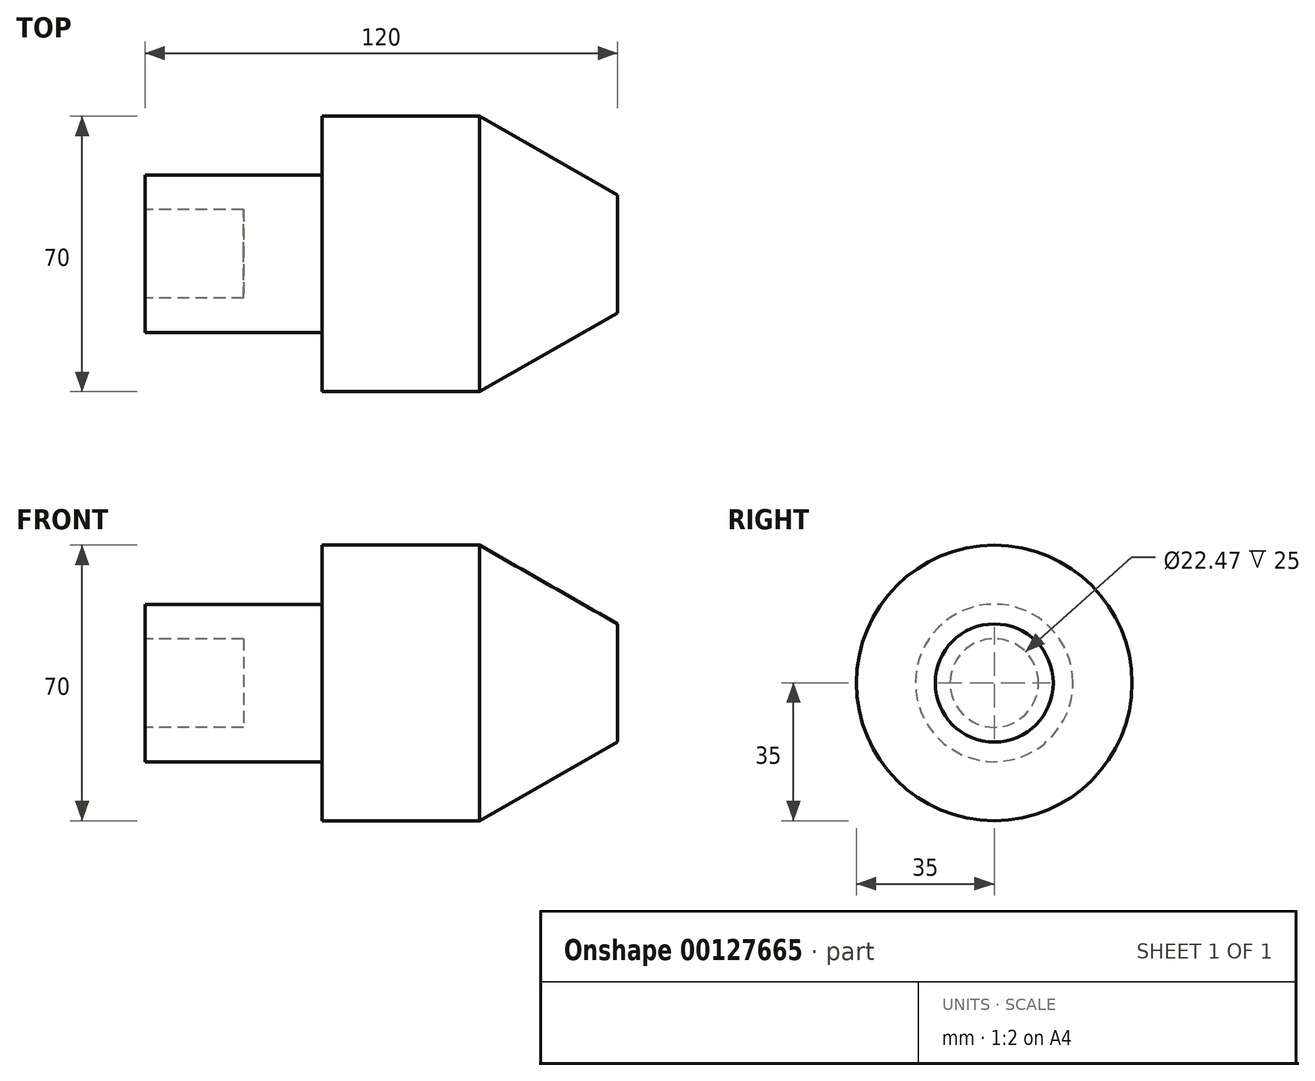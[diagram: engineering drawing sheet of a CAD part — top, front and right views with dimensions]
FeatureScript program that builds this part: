
annotation { "Feature Type Name" : "Feature", "Feature Type Description" : "" }
export const myFeature = defineFeature(function(context is Context, id is Id, definition is map)
    precondition{}
    {
        {
            var Q0;
            Q0=qCreatedBy(makeId("Front.planeOp"),FACE);
            var sketch = newSketch(context, id + "F0", { "sketchPlane" : qUnion([Q0])});
            skLineSegment(sketch, "E0", {"start": v(0, 0) * mm, "end": v(120, 0) * mm});
            skLineSegment(sketch, "E1", {"start": v(0, 0) * mm, "end": v(0, 20) * mm});
            skLineSegment(sketch, "E2", {"start": v(0, 20) * mm, "end": v(45, 20) * mm});
            skLineSegment(sketch, "E3", {"start": v(45, 20) * mm, "end": v(45, 35) * mm});
            skLineSegment(sketch, "E4", {"start": v(45, 35) * mm, "end": v(85, 35) * mm});
            skLineSegment(sketch, "E5", {"start": v(85, 35) * mm, "end": v(120, 15) * mm});
            skLineSegment(sketch, "E6", {"start": v(120, 15) * mm, "end": v(120, 0) * mm});
            skSolve(sketch);
        }
        {
            var Q0;
            Q0 = qSketchRegion(id + "F0", true);
            var Q1;
            Q1=sQuery(id+"F0.wireOp",EDGE,"E0");
            revolve(context, id + "F1", {"entities" : qUnion([Q0]), "axis" : qUnion([Q1]), "revolveType" : RevolveType.FULL});
        }
        {
            var Q0;
            Q0=makeQuery(id+"F1.opRevolve","SWEPT_FACE",FACE,{"disambiguationData":[OSD([sQuery(id+"F0.wireOp",EDGE,"E1")])]});
            var sketch = newSketch(context, id + "F2", { "sketchPlane" : qUnion([Q0])});
            skCircle(sketch, "E7", {"center": v(0, 0) * mm, "radius": 11.23 * mm});
            skSolve(sketch);
        }
        {
            var Q0;
            Q0 = qSketchRegion(id + "F2", true);
            extrude(context, id + "F3", {"entities" : qUnion([Q0]), "operationType" : NewBodyOperationType.REMOVE, "oppositeDirection" : true, "depth" : 25 * mm});
        }
    });
